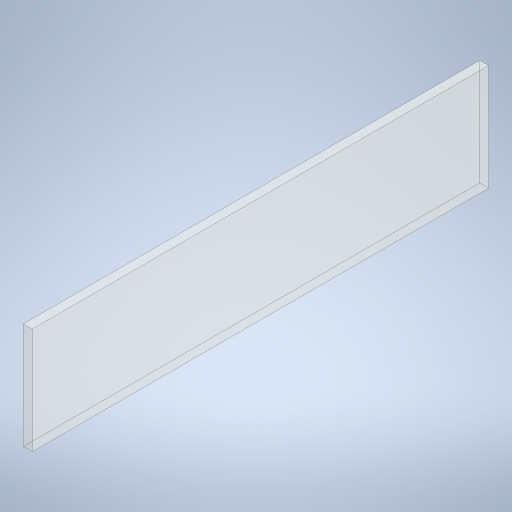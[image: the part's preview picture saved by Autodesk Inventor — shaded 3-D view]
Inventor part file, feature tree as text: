
AUTODESK INVENTOR PART (.ipt)
format: ipt  version: 2024 (Build 280153000, 153)  size: 226,304 bytes
history: native  units: in
note: dims shown in document units (in); Inventor stores cm internally (conversion verified against a paired STEP export)
features: extrude x1, sketch x1
ambient origin geometry x8: Origin, YZ Plane, XZ Plane, XY Plane, X Axis, Y Axis, Z Axis, Center Point
bodies: Body1 (feature_tree)
feature tree (2):
  extrude  "Extrusion3"  Depth=8.0315in
  sketch  "Sketch3"  dims[d8=1.8701in d9=8.0315in d10=0.1575in d11=0.0in]
